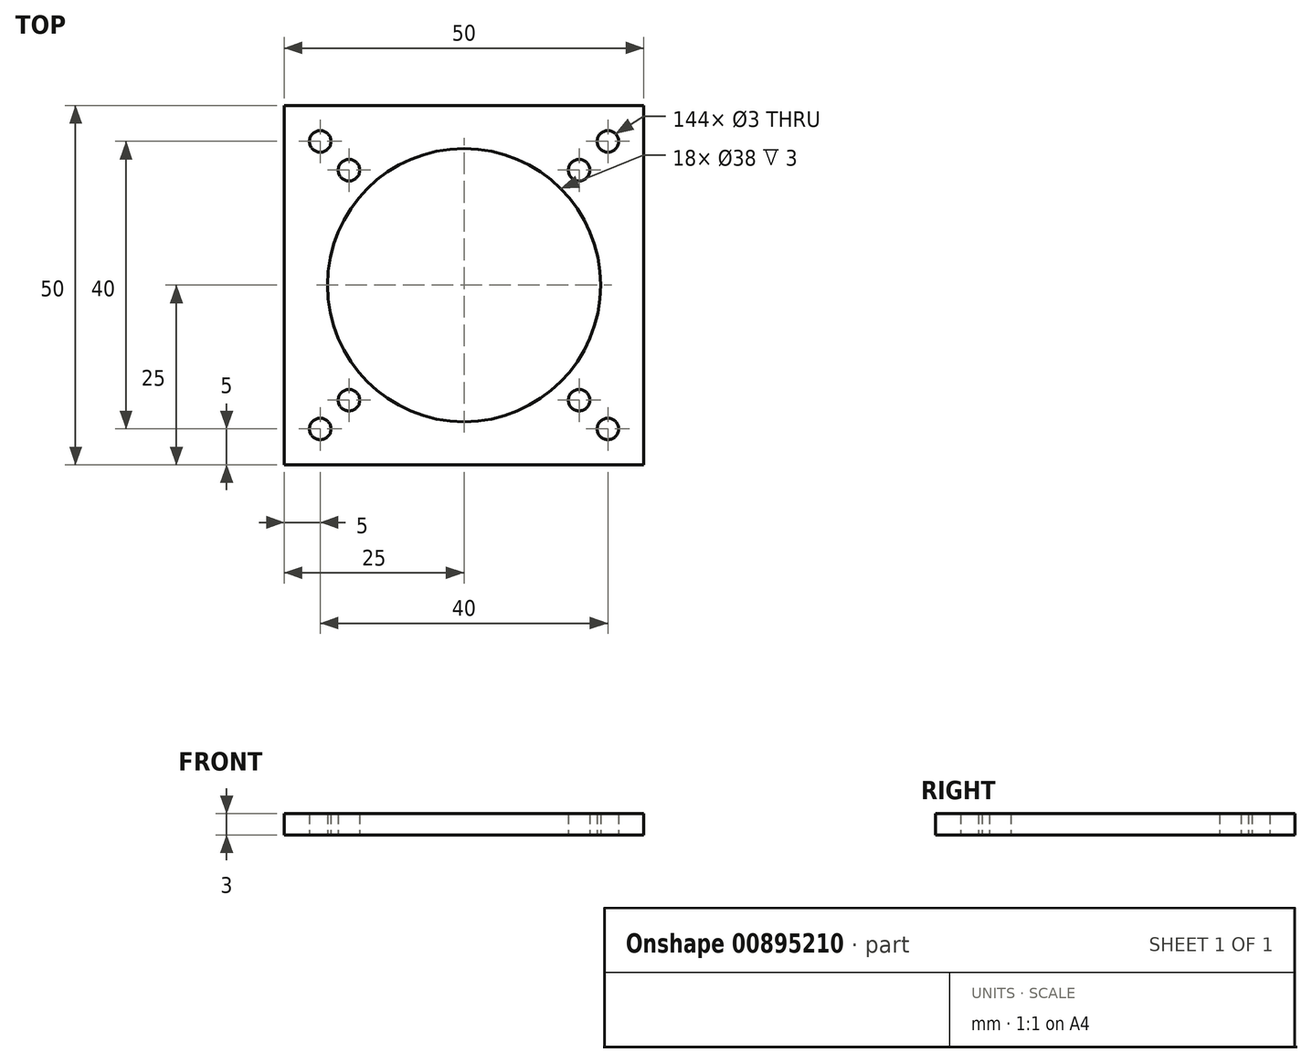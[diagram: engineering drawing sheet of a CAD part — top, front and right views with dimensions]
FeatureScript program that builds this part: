
annotation { "Feature Type Name" : "Feature", "Feature Type Description" : "" }
export const myFeature = defineFeature(function(context is Context, id is Id, definition is map)
    precondition{}
    {
        {
            var Q0;
            Q0=qCreatedBy(makeId("Top.planeOp"),FACE);
            var sketch = newSketch(context, id + "F0", { "sketchPlane" : qUnion([Q0])});
            skLineSegment(sketch, "E0.bottom", {"start": v(25, 25) * mm, "end": v(-25, 25) * mm});
            skLineSegment(sketch, "E0.top", {"start": v(25, -25) * mm, "end": v(-25, -25) * mm});
            skLineSegment(sketch, "E0.left", {"start": v(25, 25) * mm, "end": v(25, -25) * mm});
            skLineSegment(sketch, "E0.right", {"start": v(-25, 25) * mm, "end": v(-25, -25) * mm});
            skPoint(sketch, "E0.middle", {"position": v(0, 0) * mm});
            skCircle(sketch, "E1", {"center": v(-16, 16) * mm, "radius": 1.5 * mm});
            skCircle(sketch, "E2.0.1.0", {"center": v(-16, -16) * mm, "radius": 1.5 * mm});
            skCircle(sketch, "E2.1.0.0", {"center": v(16, 16) * mm, "radius": 1.5 * mm});
            skCircle(sketch, "E2.1.1.0", {"center": v(16, -16) * mm, "radius": 1.5 * mm});
            skLineSegment(sketch, "E2.direction1", {"start": v(-16, 16) * mm, "end": v(16, 16) * mm, "construction": true});
            skLineSegment(sketch, "E2.direction2", {"start": v(-16, 16) * mm, "end": v(-16, -16) * mm, "construction": true});
            skCircle(sketch, "E3", {"center": v(-20, 20) * mm, "radius": 1.5 * mm});
            skCircle(sketch, "E4.0.1.0", {"center": v(-20, -20) * mm, "radius": 1.5 * mm});
            skCircle(sketch, "E4.1.0.0", {"center": v(20, 20) * mm, "radius": 1.5 * mm});
            skCircle(sketch, "E4.1.1.0", {"center": v(20, -20) * mm, "radius": 1.5 * mm});
            skLineSegment(sketch, "E4.direction1", {"start": v(-20, 20) * mm, "end": v(20, 20) * mm, "construction": true});
            skLineSegment(sketch, "E4.direction2", {"start": v(-20, 20) * mm, "end": v(-20, -20) * mm, "construction": true});
            skCircle(sketch, "E5", {"center": v(0, 0) * mm, "radius": 19 * mm});
            skSolve(sketch);
        }
        {
            var Q0;
            Q0=makeQuery(id+"F0.imprint","IMPRINT",FACE,{"disambiguationData":[TD([[makeQuery(id+"F0.imprint","IMPRINT",EDGE,{"derivedFrom":sQuery(id+"F0.wireOp",EDGE,"E0.bottom")}),1.0]])]});
            extrude(context, id + "F1", {"entities" : qUnion([Q0]), "depth" : 3 * mm, "offsetDistance" : 25 * mm});
        }
    });
